# Revit family: QF_FESTIVE_RC6
name_source: partatom
category: Specialty Equipment
units: mm (PartAtom-declared; Revit-internal decimal feet)

## family parameters
Always vertical = Yes
Cut with Voids When Loaded = No
Part Type = Normal
Room Calculation Point = No
Round Connector Dimension = Use Diameter
Shared = No
Work Plane-Based = No

## types (1)
- RC6_220-240/50/1
    Apparent Power = 726 VA
    Conn Conduit = Yes
    Conn Plug = 10A Plug
    Control Panel A = Yes
    Control Panel B = No
    Cycle = 50 Hz
    Default Elevation = 0 mm  [stored 0 ft]
    Depth = 640 mm  [stored 2.09974 ft]
    Description = REGENT: CHILLED
    Elec Conn Connection Height = 0 mm  [stored 0 ft]
    Elec Conn RI Height = 0 mm  [stored 0 ft]
    FL Amps = 3 A
    Foodservice Equipment Identifier = Yes
    Height = 1095 mm
    Identify Quantity as Lot = Yes
    Length = 600 mm  [stored 1.9685 ft]
    Manufacturer = FESTIVE
    Max Overcurrent Protection = 0 A
    Min Ckt Ampacity = 0 A
    Model = RC6
    Number of Poles = 1
    Offset = 169 mm
    Pan 2 = No
    Pan 3 = No
    Pan Length = 570 mm  [stored 1.87008 ft]
    Panel Length = 262 mm  [stored 0.85958 ft]
    Panel Offset = 144 mm  [stored 0.472441 ft]
    Phase = 1
    Shelf 2 = No
    Volts = 220 V
    Watts = 726 W
    Weight in Kilograms = 115

note: [stored X ft] marks values corroborated as IEEE doubles in the binary element streams (Revit-internal decimal feet)

## geometry (parser evidence)
native form markers: Sweep x11
no freeform markers — native parametric forms only
